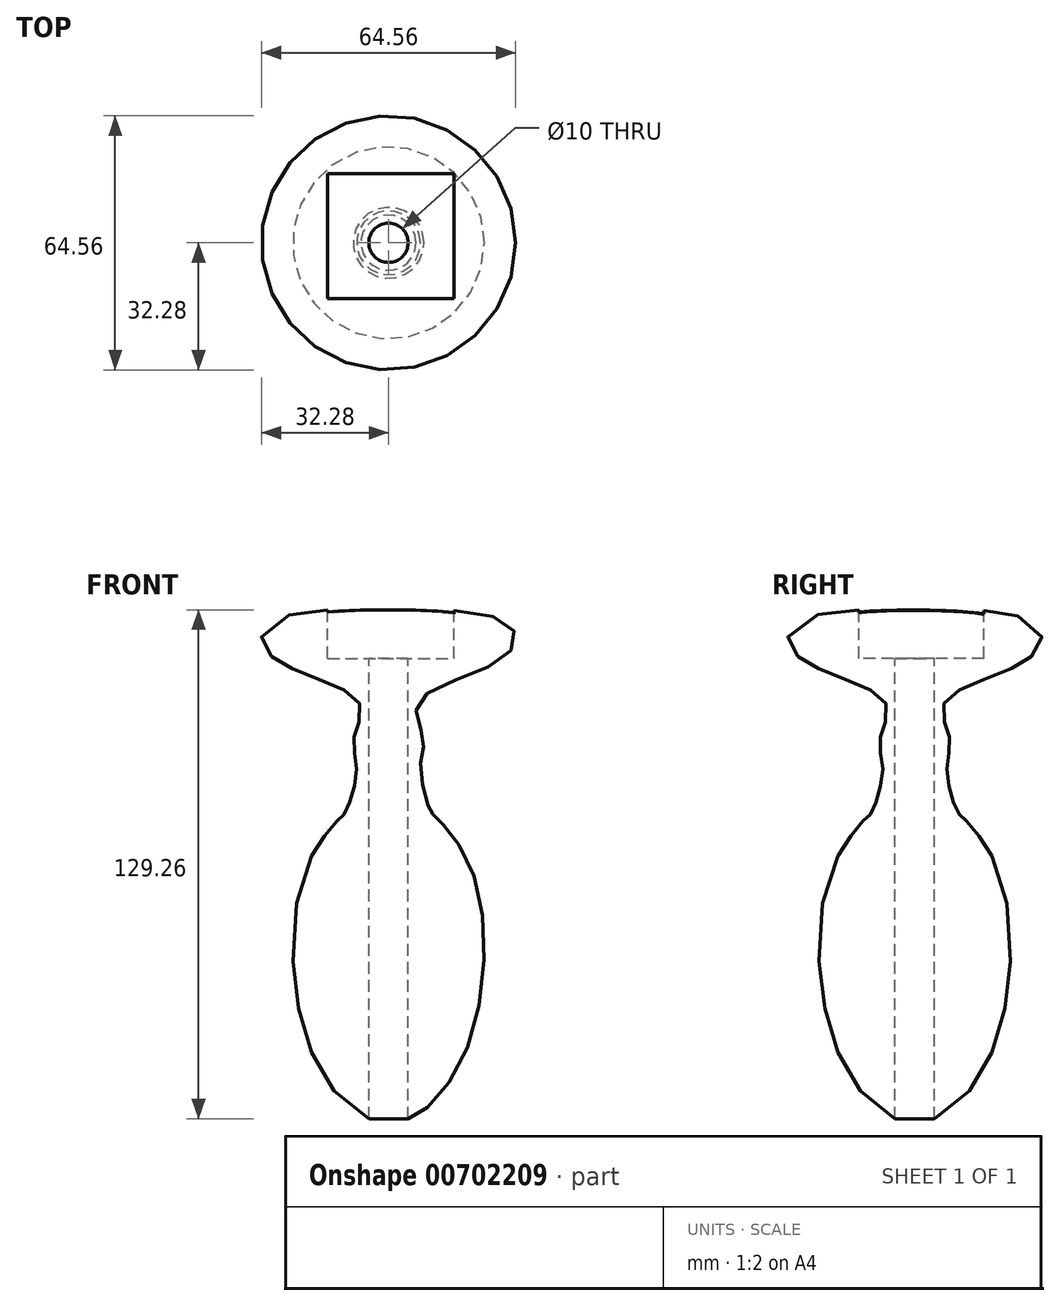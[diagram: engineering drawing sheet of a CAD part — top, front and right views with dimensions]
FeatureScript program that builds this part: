
annotation { "Feature Type Name" : "Feature", "Feature Type Description" : "" }
export const myFeature = defineFeature(function(context is Context, id is Id, definition is map)
    precondition{}
    {
        {
            var Q0;
            Q0=qCreatedBy(makeId("Front.planeOp"),FACE);
            var sketch = newSketch(context, id + "F0", { "sketchPlane" : qUnion([Q0])});
            skLineSegment(sketch, "E0", {"start": v(0, 90.47) * mm, "end": v(0, -59.53) * mm});
            skFitSpline(sketch, "E1", {"points": [v(0, -48.47) * mm, v(4, -51.76) * mm, v(18.82, -36.4) * mm, v(21.3, 11.07) * mm, v(11.68, 25.35) * mm, v(10.58, 26.73) * mm, v(8.11, 37.7) * mm, v(8.94, 44.57) * mm, v(7.56, 54.18) * mm, v(29.53, 65.69) * mm, v(29.8, 74.47) * mm, v(0, 76.14) * mm, v(0, 74.77) * mm], "startDerivative": vector(61.25, -91.31) * mm, "endDerivative": vector(30.39, -52.6) * mm});
            skSolve(sketch);
        }
        {
            var Q0;
            {var subQ0=sQuery(id+"F0.wireOp",EDGE,"E1");var subQ1=sQuery(id+"F0.wireOp",EDGE,"E0");var subQ2=makeQuery(id+"F0.imprint","INTERSECT",VERTEX,{"disambiguationData":[OD(1.0)],"derivedFrom":[subQ1,subQ0]});Q0=makeQuery(id+"F0.imprint","IMPRINT",FACE,{"disambiguationData":[TD([[makeQuery(id+"F0.imprint","IMPRINT",EDGE,{"disambiguationData":[TD([[subQ2,1.0]])],"derivedFrom":subQ1}),1.0]])]});}
            var Q1;
            Q1=sQuery(id+"F0.wireOp",EDGE,"E0");
            revolve(context, id + "F1", {"entities" : qUnion([Q0]), "axis" : qUnion([Q1]), "revolveType" : RevolveType.FULL});
        }
        {
            var Q0;
            Q0=qCreatedBy(makeId("Top.planeOp"),FACE);
            cPlane(context, id + "F2", {"entities" : qUnion([Q0]), "cplaneType" : CPlaneType.OFFSET, "offset" : 83.8 * mm, "width" : 150 * mm, "height" : 150 * mm});
        }
        {
            var Q0;
            Q0=qCreatedBy(id+"F2.planeOp",FACE);
            var sketch = newSketch(context, id + "F3", { "sketchPlane" : qUnion([Q0])});
            skLineSegment(sketch, "E2.bottom", {"start": v(-15.48, 17.54) * mm, "end": v(16.6, 17.54) * mm});
            skLineSegment(sketch, "E2.top", {"start": v(-15.48, -14.16) * mm, "end": v(16.6, -14.16) * mm});
            skLineSegment(sketch, "E2.left", {"start": v(-15.48, 17.54) * mm, "end": v(-15.48, -14.16) * mm});
            skLineSegment(sketch, "E2.right", {"start": v(16.6, 17.54) * mm, "end": v(16.6, -14.16) * mm});
            skSolve(sketch);
        }
        {
            var Q0;
            Q0=makeQuery(id+"F3.imprint","IMPRINT",FACE,{"disambiguationData":[TD([[makeQuery(id+"F3.imprint","IMPRINT",EDGE,{"derivedFrom":sQuery(id+"F3.wireOp",EDGE,"E2.bottom")}),-1.0]])]});
            extrude(context, id + "F4", {"entities" : qUnion([Q0]), "operationType" : NewBodyOperationType.REMOVE, "oppositeDirection" : true, "depth" : 18.5 * mm, "offsetDistance" : 25 * mm});
        }
        {
            var Q0;
            Q0=qCreatedBy(id+"F2.planeOp",FACE);
            var sketch = newSketch(context, id + "F5", { "sketchPlane" : qUnion([Q0])});
            skCircle(sketch, "E3", {"center": v(0, 0) * mm, "radius": 5 * mm});
            skSolve(sketch);
        }
        {
            var Q0;
            Q0=makeQuery(id+"F5.imprint","IMPRINT",FACE,{"disambiguationData":[TD([[makeQuery(id+"F5.imprint","IMPRINT",EDGE,{"derivedFrom":sQuery(id+"F5.wireOp",EDGE,"E3")}),1.0]])]});
            var Q1;
            Q1=sQuery(id+"F5.wireOp",EDGE,"E3");
            extrude(context, id + "F6", {"entities" : qUnion([Q0]), "operationType" : NewBodyOperationType.REMOVE, "surfaceEntities" : qUnion([Q1]), "oppositeDirection" : true, "depth" : 172.9 * mm, "offsetDistance" : 25 * mm});
        }
    });
